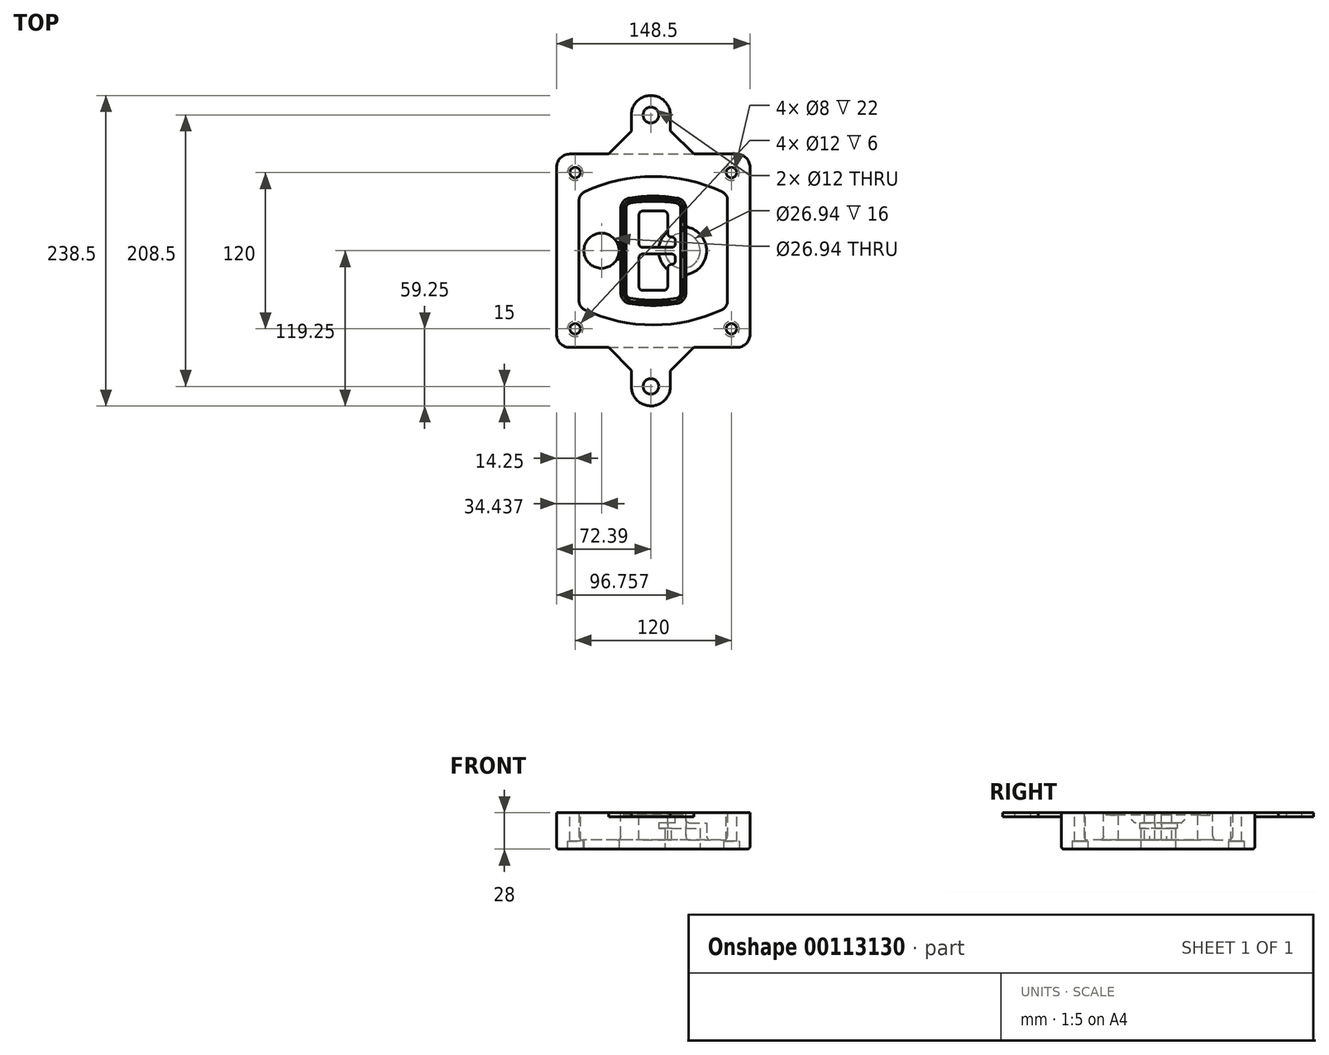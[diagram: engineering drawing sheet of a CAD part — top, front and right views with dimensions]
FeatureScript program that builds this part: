
annotation { "Feature Type Name" : "Feature", "Feature Type Description" : "" }
export const myFeature = defineFeature(function(context is Context, id is Id, definition is map)
    precondition{}
    {
        {
            var Q0;
            Q0=qCreatedBy(makeId("Top.planeOp"),FACE);
            var sketch = newSketch(context, id + "F0", { "sketchPlane" : qUnion([Q0])});
            skPoint(sketch, "E0.rect.middle", {"position": v(0, 0) * mm});
            skLineSegment(sketch, "E1.bottom", {"start": v(-64.25, -74.25) * mm, "end": v(64.25, -74.25) * mm});
            skLineSegment(sketch, "E1.top", {"start": v(-64.25, 74.25) * mm, "end": v(64.25, 74.25) * mm});
            skLineSegment(sketch, "E1.left", {"start": v(-74.25, -64.25) * mm, "end": v(-74.25, 64.25) * mm});
            skLineSegment(sketch, "E1.right", {"start": v(74.25, -64.25) * mm, "end": v(74.25, 64.25) * mm});
            skLineSegment(sketch, "E2", {"start": v(-74.25, 74.25) * mm, "end": v(74.25, -74.25) * mm, "construction": true});
            skLineSegment(sketch, "E3", {"start": v(74.25, 74.25) * mm, "end": v(-74.25, -74.25) * mm, "construction": true});
            skCircle(sketch, "E4", {"center": v(-60, 60) * mm, "radius": 4 * mm});
            skCircle(sketch, "E5", {"center": v(60, 60) * mm, "radius": 4 * mm});
            skCircle(sketch, "E6", {"center": v(60, -60) * mm, "radius": 4 * mm});
            skCircle(sketch, "E7", {"center": v(-60, -60) * mm, "radius": 4 * mm});
            skLineSegment(sketch, "E8", {"start": v(-60, 60) * mm, "end": v(60, 60) * mm, "construction": true});
            skLineSegment(sketch, "E9", {"start": v(60, 60) * mm, "end": v(60, -60) * mm, "construction": true});
            skLineSegment(sketch, "E10", {"start": v(60, -60) * mm, "end": v(-60, -60) * mm, "construction": true});
            skLineSegment(sketch, "E11", {"start": v(-60, -60) * mm, "end": v(-60, 60) * mm, "construction": true});
            skLineSegment(sketch, "E12", {"start": v(-60, 38.83) * mm, "end": v(-60, -38.83) * mm});
            skLineSegment(sketch, "E13", {"start": v(60, 38.83) * mm, "end": v(60, -38.83) * mm});
            skArc(sketch, "E14", {"start": v(54.26, 47.88) * mm, "mid": v(0, 60) * mm, "end": v(-54.26, 47.88) * mm});
            skArc(sketch, "E15", {"start": v(-54.26, -47.88) * mm, "mid": v(0, -60) * mm, "end": v(54.26, -47.88) * mm});
            skLineSegment(sketch, "E16", {"start": v(-60, 0) * mm, "end": v(60, 0) * mm, "construction": true});
            skPoint(sketch, "E17.visualSharp", {"position": v(-60, -45) * mm});
            skArc(sketch, "E17.filletArc", {"start": v(-60, -38.83) * mm, "mid": v(-58.44, -44.2) * mm, "end": v(-54.26, -47.88) * mm});
            skPoint(sketch, "E18.visualSharp", {"position": v(-60, 45) * mm});
            skArc(sketch, "E18.filletArc", {"start": v(-54.26, 47.88) * mm, "mid": v(-58.44, 44.2) * mm, "end": v(-60, 38.83) * mm});
            skPoint(sketch, "E19.visualSharp", {"position": v(60, 45) * mm});
            skArc(sketch, "E19.filletArc", {"start": v(60, 38.83) * mm, "mid": v(58.44, 44.2) * mm, "end": v(54.26, 47.88) * mm});
            skPoint(sketch, "E20.visualSharp", {"position": v(60, -45) * mm});
            skArc(sketch, "E20.filletArc", {"start": v(54.26, -47.88) * mm, "mid": v(58.44, -44.2) * mm, "end": v(60, -38.83) * mm});
            skPoint(sketch, "E21.visualSharp", {"position": v(-74.25, 74.25) * mm});
            skArc(sketch, "E21.filletArc", {"start": v(-64.25, 74.25) * mm, "mid": v(-71.32, 71.32) * mm, "end": v(-74.25, 64.25) * mm});
            skPoint(sketch, "E22.visualSharp", {"position": v(74.25, 74.25) * mm});
            skArc(sketch, "E22.filletArc", {"start": v(74.25, 64.25) * mm, "mid": v(71.32, 71.32) * mm, "end": v(64.25, 74.25) * mm});
            skPoint(sketch, "E23.visualSharp", {"position": v(74.25, -74.25) * mm});
            skArc(sketch, "E23.filletArc", {"start": v(64.25, -74.25) * mm, "mid": v(71.32, -71.32) * mm, "end": v(74.25, -64.25) * mm});
            skPoint(sketch, "E24.visualSharp", {"position": v(-74.25, -74.25) * mm});
            skArc(sketch, "E24.filletArc", {"start": v(-74.25, -64.25) * mm, "mid": v(-71.32, -71.32) * mm, "end": v(-64.25, -74.25) * mm});
            skArc(sketch, "E25.0", {"start": v(57, 38.83) * mm, "mid": v(55.9, 42.58) * mm, "end": v(52.98, 45.17) * mm});
            skLineSegment(sketch, "E25.1", {"start": v(57, 38.83) * mm, "end": v(57, -38.83) * mm});
            skArc(sketch, "E25.2", {"start": v(52.98, -45.17) * mm, "mid": v(55.9, -42.58) * mm, "end": v(57, -38.83) * mm});
            skArc(sketch, "E25.3", {"start": v(-52.98, -45.17) * mm, "mid": v(0, -57) * mm, "end": v(52.98, -45.17) * mm});
            skArc(sketch, "E25.4", {"start": v(-57, -38.83) * mm, "mid": v(-55.9, -42.58) * mm, "end": v(-52.98, -45.17) * mm});
            skArc(sketch, "E25.5", {"start": v(52.98, 45.17) * mm, "mid": v(0, 57) * mm, "end": v(-52.98, 45.17) * mm});
            skLineSegment(sketch, "E25.6", {"start": v(-57, 38.83) * mm, "end": v(-57, -38.83) * mm});
            skArc(sketch, "E25.7", {"start": v(-52.98, 45.17) * mm, "mid": v(-55.9, 42.58) * mm, "end": v(-57, 38.83) * mm});
            skArc(sketch, "E26.0", {"start": v(-55.96, 51.5) * mm, "mid": v(-61.82, 46.33) * mm, "end": v(-64, 38.83) * mm});
            skArc(sketch, "E26.1", {"start": v(55.96, 51.5) * mm, "mid": v(0, 64) * mm, "end": v(-55.96, 51.5) * mm});
            skArc(sketch, "E26.2", {"start": v(64, 38.83) * mm, "mid": v(61.82, 46.33) * mm, "end": v(55.96, 51.5) * mm});
            skLineSegment(sketch, "E26.3", {"start": v(64, 38.83) * mm, "end": v(64, -38.83) * mm});
            skArc(sketch, "E26.4", {"start": v(55.96, -51.5) * mm, "mid": v(61.82, -46.33) * mm, "end": v(64, -38.83) * mm});
            skLineSegment(sketch, "E26.5", {"start": v(-64, 38.83) * mm, "end": v(-64, -38.83) * mm});
            skArc(sketch, "E26.6", {"start": v(-55.96, -51.5) * mm, "mid": v(0, -64) * mm, "end": v(55.96, -51.5) * mm});
            skArc(sketch, "E26.7", {"start": v(-64, -38.83) * mm, "mid": v(-61.82, -46.33) * mm, "end": v(-55.96, -51.5) * mm});
            skSolve(sketch);
        }
        {
            var Q0;
            Q0=makeQuery(id+"F0.imprint","IMPRINT",FACE,{"disambiguationData":[TD([[makeQuery(id+"F0.imprint","IMPRINT",EDGE,{"derivedFrom":sQuery(id+"F0.wireOp",EDGE,"E1.bottom")}),1.0]])]});
            var Q1;
            Q1=makeQuery(id+"F0.imprint","IMPRINT",FACE,{"disambiguationData":[TD([[makeQuery(id+"F0.imprint","IMPRINT",EDGE,{"derivedFrom":sQuery(id+"F0.wireOp",EDGE,"E12")}),1.0]])]});
            var Q2;
            Q2=makeQuery(id+"F0.imprint","IMPRINT",FACE,{"disambiguationData":[TD([[makeQuery(id+"F0.imprint","IMPRINT",EDGE,{"derivedFrom":sQuery(id+"F0.wireOp",EDGE,"E25.0")}),1.0]])]});
            var Q3;
            Q3=makeQuery(id+"F0.imprint","IMPRINT",FACE,{"disambiguationData":[TD([[makeQuery(id+"F0.imprint","IMPRINT",EDGE,{"derivedFrom":sQuery(id+"F0.wireOp",EDGE,"E12")}),-1.0]])]});
            extrude(context, id + "F1", {"entities" : qUnion([Q0, Q1, Q2, Q3]), "oppositeDirection" : true, "depth" : 25 * mm});
        }
        {
            var Q0;
            Q0=makeQuery(id+"F0.imprint","IMPRINT",FACE,{"disambiguationData":[TD([[makeQuery(id+"F0.imprint","IMPRINT",EDGE,{"derivedFrom":sQuery(id+"F0.wireOp",EDGE,"E12")}),1.0]])]});
            extrude(context, id + "F2", {"entities" : qUnion([Q0]), "operationType" : NewBodyOperationType.ADD, "depth" : 3 * mm});
        }
        {
            var Q0;
            Q0=makeQuery(id+"F0.imprint","IMPRINT",FACE,{"disambiguationData":[TD([[makeQuery(id+"F0.imprint","IMPRINT",EDGE,{"derivedFrom":sQuery(id+"F0.wireOp",EDGE,"E25.0")}),1.0]])]});
            extrude(context, id + "F3", {"entities" : qUnion([Q0]), "operationType" : NewBodyOperationType.REMOVE, "oppositeDirection" : true, "depth" : 18 * mm});
        }
        {
            var Q0;
            Q0=makeQuery(id+"F2.opExtrude","CAP_FACE",FACE,{"disambiguationData":[OSD([sQuery(id+"F0.wireOp",EDGE,"E12"),sQuery(id+"F0.wireOp",EDGE,"E13"),sQuery(id+"F0.wireOp",EDGE,"E14"),sQuery(id+"F0.wireOp",EDGE,"E15"),sQuery(id+"F0.wireOp",EDGE,"E17.filletArc"),sQuery(id+"F0.wireOp",EDGE,"E18.filletArc"),sQuery(id+"F0.wireOp",EDGE,"E19.filletArc"),sQuery(id+"F0.wireOp",EDGE,"E20.filletArc"),sQuery(id+"F0.wireOp",EDGE,"E25.0"),sQuery(id+"F0.wireOp",EDGE,"E25.1"),sQuery(id+"F0.wireOp",EDGE,"E25.2"),sQuery(id+"F0.wireOp",EDGE,"E25.3"),sQuery(id+"F0.wireOp",EDGE,"E25.4"),sQuery(id+"F0.wireOp",EDGE,"E25.5"),sQuery(id+"F0.wireOp",EDGE,"E25.6"),sQuery(id+"F0.wireOp",EDGE,"E25.7")])],"isStart":false});
            var sketch = newSketch(context, id + "F4", { "sketchPlane" : qUnion([Q0])});
            skArc(sketch, "E27.0", {"start": v(-18.34, -40.45) * mm, "mid": v(0, -42) * mm, "end": v(18.34, -40.45) * mm});
            skArc(sketch, "E28.0", {"start": v(18.34, 40.45) * mm, "mid": v(0, 42) * mm, "end": v(-18.34, 40.45) * mm});
            skLineSegment(sketch, "E29", {"start": v(-25, 32.57) * mm, "end": v(-25, -32.57) * mm});
            skLineSegment(sketch, "E30", {"start": v(25, 32.57) * mm, "end": v(25, -32.57) * mm});
            skLineSegment(sketch, "E31", {"start": v(-25, 39.1) * mm, "end": v(25, 39.1) * mm, "construction": true});
            skLineSegment(sketch, "E32", {"start": v(-25, -39.1) * mm, "end": v(25, -39.1) * mm, "construction": true});
            skPoint(sketch, "E33.visualSharp", {"position": v(-25, 39.1) * mm});
            skArc(sketch, "E33.filletArc", {"start": v(-18.34, 40.45) * mm, "mid": v(-23.11, 37.73) * mm, "end": v(-25, 32.57) * mm});
            skPoint(sketch, "E34.visualSharp", {"position": v(25, 39.1) * mm});
            skArc(sketch, "E34.filletArc", {"start": v(25, 32.57) * mm, "mid": v(23.11, 37.73) * mm, "end": v(18.34, 40.45) * mm});
            skPoint(sketch, "E35.visualSharp", {"position": v(25, -39.1) * mm});
            skArc(sketch, "E35.filletArc", {"start": v(18.34, -40.45) * mm, "mid": v(23.11, -37.73) * mm, "end": v(25, -32.57) * mm});
            skPoint(sketch, "E36.visualSharp", {"position": v(-25, -39.1) * mm});
            skArc(sketch, "E36.filletArc", {"start": v(-25, -32.57) * mm, "mid": v(-23.11, -37.73) * mm, "end": v(-18.34, -40.45) * mm});
            skArc(sketch, "E37.0", {"start": v(52.98, 45.17) * mm, "mid": v(0, 57) * mm, "end": v(-52.98, 45.17) * mm});
            skArc(sketch, "E37.1", {"start": v(-52.98, 45.17) * mm, "mid": v(-55.9, 42.58) * mm, "end": v(-57, 38.83) * mm});
            skLineSegment(sketch, "E37.2", {"start": v(-57, 38.83) * mm, "end": v(-57, -38.83) * mm});
            skArc(sketch, "E37.3", {"start": v(-57, -38.83) * mm, "mid": v(-55.9, -42.58) * mm, "end": v(-52.98, -45.17) * mm});
            skArc(sketch, "E37.4", {"start": v(-52.98, -45.17) * mm, "mid": v(0, -57) * mm, "end": v(52.98, -45.17) * mm});
            skArc(sketch, "E37.5", {"start": v(52.98, -45.17) * mm, "mid": v(55.9, -42.58) * mm, "end": v(57, -38.83) * mm});
            skLineSegment(sketch, "E37.6", {"start": v(57, 38.83) * mm, "end": v(57, -38.83) * mm});
            skArc(sketch, "E37.7", {"start": v(57, 38.83) * mm, "mid": v(55.9, 42.58) * mm, "end": v(52.98, 45.17) * mm});
            skLineSegment(sketch, "E38.0", {"start": v(23, 32.57) * mm, "end": v(23, -32.57) * mm});
            skArc(sketch, "E38.1", {"start": v(18, -38.48) * mm, "mid": v(21.58, -36.44) * mm, "end": v(23, -32.57) * mm});
            skArc(sketch, "E38.2", {"start": v(-18, -38.48) * mm, "mid": v(0, -40) * mm, "end": v(18, -38.48) * mm});
            skArc(sketch, "E38.3", {"start": v(-23, -32.57) * mm, "mid": v(-21.58, -36.44) * mm, "end": v(-18, -38.48) * mm});
            skLineSegment(sketch, "E38.4", {"start": v(-23, 32.57) * mm, "end": v(-23, -32.57) * mm});
            skArc(sketch, "E38.5", {"start": v(23, 32.57) * mm, "mid": v(21.58, 36.44) * mm, "end": v(18, 38.48) * mm});
            skArc(sketch, "E38.6", {"start": v(-18, 38.48) * mm, "mid": v(-21.58, 36.44) * mm, "end": v(-23, 32.57) * mm});
            skArc(sketch, "E38.7", {"start": v(18, 38.48) * mm, "mid": v(0, 40) * mm, "end": v(-18, 38.48) * mm});
            skArc(sketch, "E39.0", {"start": v(21, 32.57) * mm, "mid": v(20.06, 35.15) * mm, "end": v(17.67, 36.5) * mm});
            skLineSegment(sketch, "E39.1", {"start": v(21, 32.57) * mm, "end": v(21, -32.57) * mm});
            skArc(sketch, "E39.2", {"start": v(17.67, -36.5) * mm, "mid": v(20.06, -35.15) * mm, "end": v(21, -32.57) * mm});
            skArc(sketch, "E39.3", {"start": v(-17.67, -36.5) * mm, "mid": v(0, -38) * mm, "end": v(17.67, -36.5) * mm});
            skArc(sketch, "E39.4", {"start": v(-21, -32.57) * mm, "mid": v(-20.06, -35.15) * mm, "end": v(-17.67, -36.5) * mm});
            skArc(sketch, "E39.5", {"start": v(17.67, 36.5) * mm, "mid": v(0, 38) * mm, "end": v(-17.67, 36.5) * mm});
            skLineSegment(sketch, "E39.6", {"start": v(-21, 32.57) * mm, "end": v(-21, -32.57) * mm});
            skArc(sketch, "E39.7", {"start": v(-17.67, 36.5) * mm, "mid": v(-20.06, 35.15) * mm, "end": v(-21, 32.57) * mm});
            skLineSegment(sketch, "E40", {"start": v(-25, 0) * mm, "end": v(25, 0) * mm, "construction": true});
            skLineSegment(sketch, "E41", {"start": v(-11, 5.5) * mm, "end": v(-11, 27.5) * mm});
            skLineSegment(sketch, "E42", {"start": v(-8, 30.5) * mm, "end": v(8, 30.5) * mm});
            skLineSegment(sketch, "E43", {"start": v(11, 27.5) * mm, "end": v(11, 13.5) * mm});
            skLineSegment(sketch, "E44", {"start": v(14, 10.5) * mm, "end": v(14, 10.5) * mm});
            skLineSegment(sketch, "E45", {"start": v(17, 7.5) * mm, "end": v(17, 5.5) * mm});
            skLineSegment(sketch, "E46", {"start": v(14, 2.5) * mm, "end": v(-8, 2.5) * mm});
            skPoint(sketch, "E47.visualSharp", {"position": v(-11, 30.5) * mm});
            skArc(sketch, "E47.filletArc", {"start": v(-8, 30.5) * mm, "mid": v(-10.12, 29.62) * mm, "end": v(-11, 27.5) * mm});
            skPoint(sketch, "E48.visualSharp", {"position": v(11, 30.5) * mm});
            skArc(sketch, "E48.filletArc", {"start": v(11, 27.5) * mm, "mid": v(10.12, 29.62) * mm, "end": v(8, 30.5) * mm});
            skPoint(sketch, "E49.visualSharp", {"position": v(11, 10.5) * mm});
            skArc(sketch, "E49.filletArc", {"start": v(11, 13.5) * mm, "mid": v(11.88, 11.38) * mm, "end": v(14, 10.5) * mm});
            skPoint(sketch, "E50.visualSharp", {"position": v(17, 10.5) * mm});
            skArc(sketch, "E50.filletArc", {"start": v(17, 7.5) * mm, "mid": v(16.12, 9.62) * mm, "end": v(14, 10.5) * mm});
            skPoint(sketch, "E51.visualSharp", {"position": v(17, 2.5) * mm});
            skArc(sketch, "E51.filletArc", {"start": v(14, 2.5) * mm, "mid": v(16.12, 3.38) * mm, "end": v(17, 5.5) * mm});
            skPoint(sketch, "E52.visualSharp", {"position": v(-11, 2.5) * mm});
            skArc(sketch, "E52.filletArc", {"start": v(-11, 5.5) * mm, "mid": v(-10.12, 3.38) * mm, "end": v(-8, 2.5) * mm});
            skLineSegment(sketch, "E53.0.MirrorCS", {"start": v(14, -2.5) * mm, "end": v(-8, -2.5) * mm});
            skArc(sketch, "E54.0.MirrorCS", {"start": v(-11, -5.5) * mm, "mid": v(-10.12, -3.38) * mm, "end": v(-8, -2.5) * mm});
            skLineSegment(sketch, "E55.0.MirrorCS", {"start": v(-11, -5.5) * mm, "end": v(-11, -27.5) * mm});
            skArc(sketch, "E56.0.MirrorCS", {"start": v(-8, -30.5) * mm, "mid": v(-10.12, -29.62) * mm, "end": v(-11, -27.5) * mm});
            skLineSegment(sketch, "E57.0.MirrorCS", {"start": v(-8, -30.5) * mm, "end": v(8, -30.5) * mm});
            skArc(sketch, "E58.0.MirrorCS", {"start": v(11, -27.5) * mm, "mid": v(10.12, -29.62) * mm, "end": v(8, -30.5) * mm});
            skLineSegment(sketch, "E59.0.MirrorCS", {"start": v(11, -27.5) * mm, "end": v(11, -13.5) * mm});
            skArc(sketch, "E60.0.MirrorCS", {"start": v(11, -13.5) * mm, "mid": v(11.88, -11.38) * mm, "end": v(14, -10.5) * mm});
            skArc(sketch, "E61.0.MirrorCS", {"start": v(17, -7.5) * mm, "mid": v(16.12, -9.62) * mm, "end": v(14, -10.5) * mm});
            skLineSegment(sketch, "E62.0.MirrorCS", {"start": v(17, -7.5) * mm, "end": v(17, -5.5) * mm});
            skArc(sketch, "E63.0.MirrorCS", {"start": v(14, -2.5) * mm, "mid": v(16.12, -3.38) * mm, "end": v(17, -5.5) * mm});
            skSolve(sketch);
        }
        {
            var Q0;
            Q0=makeQuery(id+"F4.imprint","IMPRINT",FACE,{"disambiguationData":[TD([[makeQuery(id+"F4.imprint","IMPRINT",EDGE,{"derivedFrom":sQuery(id+"F4.wireOp",EDGE,"E27.0")}),1.0]])]});
            var Q1;
            Q1=makeQuery(id+"F4.imprint","IMPRINT",FACE,{"disambiguationData":[TD([[makeQuery(id+"F4.imprint","IMPRINT",EDGE,{"derivedFrom":sQuery(id+"F4.wireOp",EDGE,"E38.0")}),-1.0]])]});
            var Q2;
            Q2=makeQuery(id+"F4.imprint","IMPRINT",FACE,{"disambiguationData":[TD([[makeQuery(id+"F4.imprint","IMPRINT",EDGE,{"derivedFrom":sQuery(id+"F4.wireOp",EDGE,"E39.0")}),1.0]])]});
            extrude(context, id + "F5", {"entities" : qUnion([Q0, Q1, Q2]), "operationType" : NewBodyOperationType.ADD, "endBound" : BoundingType.UP_TO_NEXT, "oppositeDirection" : true, "depth" : 25 * mm});
        }
        {
            var Q0;
            Q0=makeQuery(id+"F4.imprint","IMPRINT",FACE,{"disambiguationData":[TD([[makeQuery(id+"F4.imprint","IMPRINT",EDGE,{"derivedFrom":sQuery(id+"F4.wireOp",EDGE,"E38.0")}),-1.0]])]});
            extrude(context, id + "F6", {"entities" : qUnion([Q0]), "operationType" : NewBodyOperationType.REMOVE, "oppositeDirection" : true, "depth" : 2 * mm});
        }
        {
            var Q0;
            Q0=makeQuery(id+"F1.opExtrude","CAP_FACE",FACE,{"disambiguationData":[OSD([sQuery(id+"F0.wireOp",EDGE,"E1.bottom"),sQuery(id+"F0.wireOp",EDGE,"E1.top"),sQuery(id+"F0.wireOp",EDGE,"E1.left"),sQuery(id+"F0.wireOp",EDGE,"E1.right"),sQuery(id+"F0.wireOp",EDGE,"E4"),sQuery(id+"F0.wireOp",EDGE,"E5"),sQuery(id+"F0.wireOp",EDGE,"E6"),sQuery(id+"F0.wireOp",EDGE,"E7"),sQuery(id+"F0.wireOp",EDGE,"E21.filletArc"),sQuery(id+"F0.wireOp",EDGE,"E22.filletArc"),sQuery(id+"F0.wireOp",EDGE,"E23.filletArc"),sQuery(id+"F0.wireOp",EDGE,"E24.filletArc")])],"isStart":false});
            var sketch = newSketch(context, id + "F7", { "sketchPlane" : qUnion([Q0])});
            skCircle(sketch, "E64", {"center": v(22.5, 0) * mm, "radius": 13.47 * mm});
            skCircle(sketch, "E65", {"center": v(-39.81, 0) * mm, "radius": 13.47 * mm});
            skLineSegment(sketch, "E66", {"start": v(74.25, 0) * mm, "end": v(-74.25, 0) * mm});
            skCircle(sketch, "E67", {"center": v(22.5, 0) * mm, "radius": 18.47 * mm});
            skCircle(sketch, "E68", {"center": v(60, -60) * mm, "radius": 6 * mm});
            skCircle(sketch, "E69", {"center": v(-60, -60) * mm, "radius": 6 * mm});
            skCircle(sketch, "E70", {"center": v(-60, 60) * mm, "radius": 6 * mm});
            skCircle(sketch, "E71", {"center": v(60, 60) * mm, "radius": 6 * mm});
            skSolve(sketch);
        }
        {
            var Q0;
            {var subQ1=sQuery(id+"F7.wireOp",EDGE,"E66");var subQ4=sQuery(id+"F7.wireOp",EDGE,"E64");var subQ6=makeQuery(id+"F7.imprint","INTERSECT",VERTEX,{"disambiguationData":[OD(0.0)],"derivedFrom":[subQ4,subQ1]});Q0=makeQuery(id+"F7.imprint","IMPRINT",FACE,{"disambiguationData":[TD([[makeQuery(id+"F7.imprint","IMPRINT",EDGE,{"disambiguationData":[TD([[subQ6,-1.0]])],"derivedFrom":subQ4}),-1.0]])]});}
            var Q1;
            {var subQ0=sQuery(id+"F7.wireOp",EDGE,"E66");var subQ1=sQuery(id+"F7.wireOp",EDGE,"E64");var subQ3=makeQuery(id+"F7.imprint","INTERSECT",VERTEX,{"disambiguationData":[OD(0.0)],"derivedFrom":[subQ1,subQ0]});Q1=makeQuery(id+"F7.imprint","IMPRINT",FACE,{"disambiguationData":[TD([[makeQuery(id+"F7.imprint","IMPRINT",EDGE,{"disambiguationData":[TD([[subQ3,-1.0]])],"derivedFrom":subQ1}),1.0]])]});}
            var Q2;
            {var subQ0=sQuery(id+"F7.wireOp",EDGE,"E66");var subQ1=sQuery(id+"F7.wireOp",EDGE,"E64");var subQ3=makeQuery(id+"F7.imprint","INTERSECT",VERTEX,{"disambiguationData":[OD(0.0)],"derivedFrom":[subQ1,subQ0]});Q2=makeQuery(id+"F7.imprint","IMPRINT",FACE,{"disambiguationData":[TD([[makeQuery(id+"F7.imprint","IMPRINT",EDGE,{"disambiguationData":[TD([[subQ3,1.0]])],"derivedFrom":subQ1}),1.0]])]});}
            var Q3;
            {var subQ1=sQuery(id+"F7.wireOp",EDGE,"E66");var subQ4=sQuery(id+"F7.wireOp",EDGE,"E64");var subQ6=makeQuery(id+"F7.imprint","INTERSECT",VERTEX,{"disambiguationData":[OD(0.0)],"derivedFrom":[subQ4,subQ1]});Q3=makeQuery(id+"F7.imprint","IMPRINT",FACE,{"disambiguationData":[TD([[makeQuery(id+"F7.imprint","IMPRINT",EDGE,{"disambiguationData":[TD([[subQ6,1.0]])],"derivedFrom":subQ4}),-1.0]])]});}
            extrude(context, id + "F8", {"entities" : qUnion([Q0, Q1, Q2, Q3]), "operationType" : NewBodyOperationType.ADD, "oppositeDirection" : true, "depth" : 20 * mm});
        }
        {
            var Q0;
            {var subQ0=sQuery(id+"F7.wireOp",EDGE,"E66");var subQ1=sQuery(id+"F7.wireOp",EDGE,"E64");var subQ3=makeQuery(id+"F7.imprint","INTERSECT",VERTEX,{"disambiguationData":[OD(0.0)],"derivedFrom":[subQ1,subQ0]});Q0=makeQuery(id+"F7.imprint","IMPRINT",FACE,{"disambiguationData":[TD([[makeQuery(id+"F7.imprint","IMPRINT",EDGE,{"disambiguationData":[TD([[subQ3,-1.0]])],"derivedFrom":subQ1}),1.0]])]});}
            var Q1;
            {var subQ0=sQuery(id+"F7.wireOp",EDGE,"E66");var subQ1=sQuery(id+"F7.wireOp",EDGE,"E64");var subQ3=makeQuery(id+"F7.imprint","INTERSECT",VERTEX,{"disambiguationData":[OD(0.0)],"derivedFrom":[subQ1,subQ0]});Q1=makeQuery(id+"F7.imprint","IMPRINT",FACE,{"disambiguationData":[TD([[makeQuery(id+"F7.imprint","IMPRINT",EDGE,{"disambiguationData":[TD([[subQ3,1.0]])],"derivedFrom":subQ1}),1.0]])]});}
            extrude(context, id + "F9", {"entities" : qUnion([Q0, Q1]), "operationType" : NewBodyOperationType.REMOVE, "oppositeDirection" : true, "depth" : 16 * mm});
        }
        {
            var Q0;
            {var subQ0=sQuery(id+"F7.wireOp",EDGE,"E66");var subQ1=sQuery(id+"F7.wireOp",EDGE,"E65");var subQ3=makeQuery(id+"F7.imprint","INTERSECT",VERTEX,{"disambiguationData":[OD(0.0)],"derivedFrom":[subQ1,subQ0]});Q0=makeQuery(id+"F7.imprint","IMPRINT",FACE,{"disambiguationData":[TD([[makeQuery(id+"F7.imprint","IMPRINT",EDGE,{"disambiguationData":[TD([[subQ3,-1.0]])],"derivedFrom":subQ1}),1.0]])]});}
            var Q1;
            {var subQ0=sQuery(id+"F7.wireOp",EDGE,"E66");var subQ1=sQuery(id+"F7.wireOp",EDGE,"E65");var subQ3=makeQuery(id+"F7.imprint","INTERSECT",VERTEX,{"disambiguationData":[OD(0.0)],"derivedFrom":[subQ1,subQ0]});Q1=makeQuery(id+"F7.imprint","IMPRINT",FACE,{"disambiguationData":[TD([[makeQuery(id+"F7.imprint","IMPRINT",EDGE,{"disambiguationData":[TD([[subQ3,1.0]])],"derivedFrom":subQ1}),1.0]])]});}
            extrude(context, id + "F10", {"entities" : qUnion([Q0, Q1]), "operationType" : NewBodyOperationType.REMOVE, "oppositeDirection" : true, "depth" : 25 * mm});
        }
        {
            var Q0;
            Q0=makeQuery(id+"F7.imprint","IMPRINT",FACE,{"disambiguationData":[TD([[makeQuery(id+"F7.imprint","IMPRINT",EDGE,{"derivedFrom":sQuery(id+"F7.wireOp",EDGE,"E68")}),1.0]])]});
            var Q1;
            Q1=makeQuery(id+"F7.imprint","IMPRINT",FACE,{"disambiguationData":[TD([[makeQuery(id+"F7.imprint","IMPRINT",EDGE,{"derivedFrom":makeQuery(id+"F1.opExtrude","CAP_EDGE",EDGE,{"disambiguationData":[OSD([sQuery(id+"F0.wireOp",EDGE,"E5")])],"isStart":false})}),-1.0]])]});
            var Q2;
            Q2=makeQuery(id+"F7.imprint","IMPRINT",FACE,{"disambiguationData":[TD([[makeQuery(id+"F7.imprint","IMPRINT",EDGE,{"derivedFrom":sQuery(id+"F7.wireOp",EDGE,"E69")}),1.0]])]});
            var Q3;
            Q3=makeQuery(id+"F7.imprint","IMPRINT",FACE,{"disambiguationData":[TD([[makeQuery(id+"F7.imprint","IMPRINT",EDGE,{"derivedFrom":makeQuery(id+"F1.opExtrude","CAP_EDGE",EDGE,{"disambiguationData":[OSD([sQuery(id+"F0.wireOp",EDGE,"E4")])],"isStart":false})}),-1.0]])]});
            var Q4;
            Q4=makeQuery(id+"F7.imprint","IMPRINT",FACE,{"disambiguationData":[TD([[makeQuery(id+"F7.imprint","IMPRINT",EDGE,{"derivedFrom":sQuery(id+"F7.wireOp",EDGE,"E70")}),1.0]])]});
            var Q5;
            Q5=makeQuery(id+"F7.imprint","IMPRINT",FACE,{"disambiguationData":[TD([[makeQuery(id+"F7.imprint","IMPRINT",EDGE,{"derivedFrom":makeQuery(id+"F1.opExtrude","CAP_EDGE",EDGE,{"disambiguationData":[OSD([sQuery(id+"F0.wireOp",EDGE,"E7")])],"isStart":false})}),-1.0]])]});
            var Q6;
            Q6=makeQuery(id+"F7.imprint","IMPRINT",FACE,{"disambiguationData":[TD([[makeQuery(id+"F7.imprint","IMPRINT",EDGE,{"derivedFrom":sQuery(id+"F7.wireOp",EDGE,"E71")}),1.0]])]});
            var Q7;
            Q7=makeQuery(id+"F7.imprint","IMPRINT",FACE,{"disambiguationData":[TD([[makeQuery(id+"F7.imprint","IMPRINT",EDGE,{"derivedFrom":makeQuery(id+"F1.opExtrude","CAP_EDGE",EDGE,{"disambiguationData":[OSD([sQuery(id+"F0.wireOp",EDGE,"E6")])],"isStart":false})}),-1.0]])]});
            extrude(context, id + "F11", {"entities" : qUnion([Q0, Q1, Q2, Q3, Q4, Q5, Q6, Q7]), "operationType" : NewBodyOperationType.REMOVE, "oppositeDirection" : true, "depth" : 6 * mm});
        }
        {
            var Q0;
            Q0=makeQuery(id+"F9.boolean.opBoolean","COPY",FACE,{"derivedFrom":makeQuery(id+"F9.opExtrude","CAP_FACE",FACE,{"disambiguationData":[OSD([sQuery(id+"F7.wireOp",EDGE,"E64")])],"isStart":false})});
            var sketch = newSketch(context, id + "F12", { "sketchPlane" : qUnion([Q0])});
            skArc(sketch, "E72.0", {"start": v(11, 14.45) * mm, "mid": v(6.45, 9.13) * mm, "end": v(4.2, 2.5) * mm});
            skArc(sketch, "E72.1", {"start": v(4.2, -2.5) * mm, "mid": v(6.45, -9.13) * mm, "end": v(11, -14.45) * mm});
            skLineSegment(sketch, "E73", {"start": v(4.2, -2.5) * mm, "end": v(14, -2.5) * mm});
            skLineSegment(sketch, "E74.0", {"start": v(14, 2.5) * mm, "end": v(4.2, 2.5) * mm});
            skArc(sketch, "E74.1", {"start": v(14, 2.5) * mm, "mid": v(16.12, 3.38) * mm, "end": v(17, 5.5) * mm});
            skLineSegment(sketch, "E74.2", {"start": v(17, 7.5) * mm, "end": v(17, 5.5) * mm});
            skArc(sketch, "E74.3", {"start": v(17, 7.5) * mm, "mid": v(16.12, 9.62) * mm, "end": v(14, 10.5) * mm});
            skArc(sketch, "E74.4", {"start": v(11, 13.5) * mm, "mid": v(11.88, 11.38) * mm, "end": v(14, 10.5) * mm});
            skLineSegment(sketch, "E74.5", {"start": v(11, 14.45) * mm, "end": v(11, 13.5) * mm});
            skLineSegment(sketch, "E74.7", {"start": v(14, -2.5) * mm, "end": v(4.2, -2.5) * mm});
            skArc(sketch, "E74.8", {"start": v(14, -2.5) * mm, "mid": v(16.12, -3.38) * mm, "end": v(17, -5.5) * mm});
            skLineSegment(sketch, "E74.9", {"start": v(17, -7.5) * mm, "end": v(17, -5.5) * mm});
            skArc(sketch, "E74.10", {"start": v(17, -7.5) * mm, "mid": v(16.12, -9.62) * mm, "end": v(14, -10.5) * mm});
            skArc(sketch, "E74.11", {"start": v(11, -13.5) * mm, "mid": v(11.88, -11.38) * mm, "end": v(14, -10.5) * mm});
            skLineSegment(sketch, "E74.12", {"start": v(11, -14.45) * mm, "end": v(11, -13.5) * mm});
            skPoint(sketch, "E75.orphan", {"position": v(11, -27.5) * mm});
            skPoint(sketch, "E76.orphan", {"position": v(-8, -2.5) * mm});
            skPoint(sketch, "E77.orphan", {"position": v(-8, 2.5) * mm});
            skPoint(sketch, "E78.orphan", {"position": v(11, 27.5) * mm});
            skSolve(sketch);
        }
        {
            var Q0;
            {var subQ7=sQuery(id+"F12.wireOp",EDGE,"E72.0");var subQ14=sQuery(id+"F12.wireOp",EDGE,"E72.1");var subQ16=sQuery(id+"F12.wireOp",EDGE,"E74.1");var subQ18=sQuery(id+"F12.wireOp",EDGE,"E74.8");Q0=qUnion([makeQuery(id+"F12.imprint","IMPRINT",FACE,{"disambiguationData":[TD([[makeQuery(id+"F12.imprint","IMPRINT",EDGE,{"derivedFrom":subQ7}),1.0]])]}),makeQuery(id+"F12.imprint","IMPRINT",FACE,{"disambiguationData":[TD([[makeQuery(id+"F12.imprint","IMPRINT",EDGE,{"derivedFrom":subQ14}),1.0]])]}),makeQuery(id+"F12.imprint","IMPRINT",FACE,{"disambiguationData":[TD([[makeQuery(id+"F12.imprint","IMPRINT",EDGE,{"derivedFrom":subQ16}),1.0]])]}),makeQuery(id+"F12.imprint","IMPRINT",FACE,{"disambiguationData":[TD([[makeQuery(id+"F12.imprint","IMPRINT",EDGE,{"derivedFrom":subQ18}),-1.0]])]})]);}
            var Q1;
            Q1=makeQuery(id+"F5.boolean.opBoolean","SPLIT",FACE,{"disambiguationData":[TD([makeQuery(id+"F5.opExtrude","SWEPT_FACE",FACE,{"disambiguationData":[OSD([sQuery(id+"F4.wireOp",EDGE,"E41")])]})])],"derivedFrom":makeQuery(id+"F3.boolean.opBoolean","COPY",FACE,{"derivedFrom":makeQuery(id+"F3.opExtrude","CAP_FACE",FACE,{"disambiguationData":[OSD([sQuery(id+"F0.wireOp",EDGE,"E25.0"),sQuery(id+"F0.wireOp",EDGE,"E25.1"),sQuery(id+"F0.wireOp",EDGE,"E25.2"),sQuery(id+"F0.wireOp",EDGE,"E25.3"),sQuery(id+"F0.wireOp",EDGE,"E25.4"),sQuery(id+"F0.wireOp",EDGE,"E25.5"),sQuery(id+"F0.wireOp",EDGE,"E25.6"),sQuery(id+"F0.wireOp",EDGE,"E25.7")])],"isStart":false})})});
            extrude(context, id + "F13", {"entities" : qUnion([Q0]), "operationType" : NewBodyOperationType.REMOVE, "endBound" : BoundingType.UP_TO_SURFACE, "endBoundEntityFace" : qUnion([Q1]), "depth" : 25 * mm});
        }
        {
            var Q0;
            Q0=makeQuery(id+"F3.boolean.opBoolean","COPY",EDGE,{"derivedFrom":makeQuery(id+"F3.opExtrude","CAP_EDGE",EDGE,{"disambiguationData":[OSD([sQuery(id+"F0.wireOp",EDGE,"E25.6")])],"isStart":false})});
            var Q1;
            Q1=makeQuery(id+"F8.boolean.opBoolean","INTERSECT",EDGE,{"derivedFrom":[makeQuery(id+"F5.opExtrude","SWEPT_FACE",FACE,{"disambiguationData":[OSD([sQuery(id+"F4.wireOp",EDGE,"E30")])]}),makeQuery(id+"F8.opExtrude","CAP_FACE",FACE,{"disambiguationData":[OSD([sQuery(id+"F7.wireOp",EDGE,"E67")])],"isStart":false})]});
            var Q2;
            Q2=makeQuery(id+"F8.boolean.opBoolean","INTERSECT",EDGE,{"disambiguationData":[OD(1.0)],"derivedFrom":[makeQuery(id+"F5.opExtrude","SWEPT_FACE",FACE,{"disambiguationData":[OSD([sQuery(id+"F4.wireOp",EDGE,"E30")])]}),makeQuery(id+"F8.opExtrude","SWEPT_FACE",FACE,{"disambiguationData":[OSD([sQuery(id+"F7.wireOp",EDGE,"E67")])]})]});
            var Q3;
            {var subQ0=sQuery(id+"F4.wireOp",EDGE,"E30");Q3=makeQuery(id+"F8.boolean.opBoolean","SPLIT",EDGE,{"disambiguationData":[TD([makeQuery(id+"F5.opExtrude","SWEPT_FACE",FACE,{"disambiguationData":[OSD([sQuery(id+"F4.wireOp",EDGE,"E35.filletArc")])]})])],"derivedFrom":makeQuery(id+"F5.opExtrude","CAP_EDGE",EDGE,{"disambiguationData":[OSD([subQ0])],"isStart":false})});}
            var Q4;
            {var subQ0=sQuery(id+"F0.wireOp",EDGE,"E25.7");var subQ1=sQuery(id+"F0.wireOp",EDGE,"E25.1");var subQ2=sQuery(id+"F0.wireOp",EDGE,"E25.6");var subQ3=sQuery(id+"F0.wireOp",EDGE,"E25.5");var subQ4=sQuery(id+"F0.wireOp",EDGE,"E25.4");var subQ5=sQuery(id+"F0.wireOp",EDGE,"E25.0");var subQ6=sQuery(id+"F0.wireOp",EDGE,"E25.2");var subQ7=sQuery(id+"F0.wireOp",EDGE,"E25.3");Q4=makeQuery(id+"F8.boolean.opBoolean","INTERSECT",EDGE,{"derivedFrom":[makeQuery(id+"F5.boolean.opBoolean","SPLIT",FACE,{"disambiguationData":[TD([makeQuery(id+"F2.opExtrude","SWEPT_FACE",FACE,{"disambiguationData":[OSD([subQ5])]})])],"derivedFrom":makeQuery(id+"F3.boolean.opBoolean","COPY",FACE,{"derivedFrom":makeQuery(id+"F3.opExtrude","CAP_FACE",FACE,{"disambiguationData":[OSD([subQ5,subQ1,subQ6,subQ7,subQ4,subQ3,subQ2,subQ0])],"isStart":false})})}),makeQuery(id+"F8.opExtrude","SWEPT_FACE",FACE,{"disambiguationData":[OSD([sQuery(id+"F7.wireOp",EDGE,"E67")])]})]});}
            var Q5;
            Q5=makeQuery(id+"F8.boolean.opBoolean","INTERSECT",EDGE,{"disambiguationData":[OD(0.0)],"derivedFrom":[makeQuery(id+"F5.opExtrude","SWEPT_FACE",FACE,{"disambiguationData":[OSD([sQuery(id+"F4.wireOp",EDGE,"E30")])]}),makeQuery(id+"F8.opExtrude","SWEPT_FACE",FACE,{"disambiguationData":[OSD([sQuery(id+"F7.wireOp",EDGE,"E67")])]})]});
            fillet(context, id + "F14", {"entities" : qUnion([Q0, Q1, Q2, Q3, Q4, Q5]), "radius" : 3 * mm, "tangentPropagation" : true, "allowEdgeOverflow" : false});
        }
        {
            var Q0;
            Q0=makeQuery(id+"F1.opExtrude","CAP_EDGE",EDGE,{"disambiguationData":[OSD([sQuery(id+"F0.wireOp",EDGE,"E1.bottom")])],"isStart":false});
            fillet(context, id + "F15", {"entities" : qUnion([Q0]), "radius" : 2 * mm, "tangentPropagation" : true, "allowEdgeOverflow" : false});
        }
        {
            var Q0;
            {var subQ0=sQuery(id+"F0.wireOp",EDGE,"E22.filletArc");var subQ1=sQuery(id+"F0.wireOp",EDGE,"E7");var subQ2=sQuery(id+"F0.wireOp",EDGE,"E6");var subQ3=sQuery(id+"F0.wireOp",EDGE,"E5");var subQ4=sQuery(id+"F0.wireOp",EDGE,"E4");var subQ5=sQuery(id+"F0.wireOp",EDGE,"E1.bottom");var subQ6=sQuery(id+"F0.wireOp",EDGE,"E21.filletArc");var subQ7=sQuery(id+"F0.wireOp",EDGE,"E1.top");var subQ8=sQuery(id+"F0.wireOp",EDGE,"E1.left");var subQ9=sQuery(id+"F0.wireOp",EDGE,"E1.right");var subQ10=sQuery(id+"F0.wireOp",EDGE,"E23.filletArc");var subQ11=sQuery(id+"F0.wireOp",EDGE,"E24.filletArc");Q0=makeQuery(id+"F2.boolean.opBoolean","SPLIT",FACE,{"disambiguationData":[TD([makeQuery(id+"F1.opExtrude","SWEPT_FACE",FACE,{"disambiguationData":[OSD([subQ5])]})])],"derivedFrom":makeQuery(id+"F1.opExtrude","CAP_FACE",FACE,{"disambiguationData":[OSD([subQ5,subQ7,subQ8,subQ9,subQ4,subQ3,subQ2,subQ1,subQ6,subQ0,subQ10,subQ11])],"isStart":true})});}
            var sketch = newSketch(context, id + "F16", { "sketchPlane" : qUnion([Q0])});
            skLineSegment(sketch, "E79.0", {"start": v(-64.25, 74.25) * mm, "end": v(64.25, 74.25) * mm});
            skPoint(sketch, "E80.endSnap0", {"position": v(0, 89.25) * mm});
            skLineSegment(sketch, "E81", {"start": v(13.14, 104.25) * mm, "end": v(13.14, 92.25) * mm});
            skLineSegment(sketch, "E82", {"start": v(13.14, 92.25) * mm, "end": v(31.14, 74.25) * mm});
            skArc(sketch, "E83", {"start": v(13.14, 104.25) * mm, "mid": v(-1.99, 119.25) * mm, "end": v(-16.86, 104) * mm});
            skCircle(sketch, "E84", {"center": v(-1.86, 104.25) * mm, "radius": 6 * mm});
            skLineSegment(sketch, "E85", {"start": v(-16.86, 104) * mm, "end": v(-16.65, 92) * mm});
            skLineSegment(sketch, "E86", {"start": v(-16.65, 92) * mm, "end": v(-34.4, 74.25) * mm});
            skLineSegment(sketch, "E87", {"start": v(0, 0) * mm, "end": v(-108.8, 0) * mm, "construction": true});
            skLineSegment(sketch, "E88.MirrorCS", {"start": v(13.14, -104.25) * mm, "end": v(13.14, -92.25) * mm});
            skCircle(sketch, "E89.MirrorC", {"center": v(-1.86, -104.25) * mm, "radius": 6 * mm});
            skLineSegment(sketch, "E90.MirrorCS", {"start": v(-16.86, -104) * mm, "end": v(-16.65, -92) * mm});
            skLineSegment(sketch, "E91.MirrorCS", {"start": v(-16.65, -92) * mm, "end": v(-34.4, -74.25) * mm});
            skLineSegment(sketch, "E92.MirrorCS", {"start": v(13.14, -92.25) * mm, "end": v(31.14, -74.25) * mm});
            skArc(sketch, "E93.MirrorCS", {"start": v(13.14, -104.25) * mm, "mid": v(-1.99, -119.25) * mm, "end": v(-16.86, -104) * mm});
            skPoint(sketch, "E94.MirrorP", {"position": v(0, -89.25) * mm});
            skSolve(sketch);
        }
        {
            var Q0;
            Q0=makeQuery(id+"F16.imprint","IMPRINT",FACE,{"disambiguationData":[TD([[makeQuery(id+"F16.imprint","IMPRINT",EDGE,{"derivedFrom":makeQuery(id+"F1.opExtrude","CAP_EDGE",EDGE,{"disambiguationData":[OSD([sQuery(id+"F0.wireOp",EDGE,"E1.left")])],"isStart":true})}),-1.0]])]});
            var Q1;
            Q1=makeQuery(id+"F16.imprint","IMPRINT",FACE,{"disambiguationData":[TD([[makeQuery(id+"F16.imprint","IMPRINT",EDGE,{"derivedFrom":sQuery(id+"F16.wireOp",EDGE,"E88.MirrorCS")}),1.0]])]});
            var Q2;
            Q2=makeQuery(id+"F16.imprint","IMPRINT",FACE,{"disambiguationData":[TD([[makeQuery(id+"F16.imprint","IMPRINT",EDGE,{"derivedFrom":sQuery(id+"F16.wireOp",EDGE,"E81")}),-1.0]])]});
            var Q3;
            Q3=makeQuery(id+"F2.opExtrude","CAP_FACE",FACE,{"disambiguationData":[OSD([sQuery(id+"F0.wireOp",EDGE,"E12"),sQuery(id+"F0.wireOp",EDGE,"E13"),sQuery(id+"F0.wireOp",EDGE,"E14"),sQuery(id+"F0.wireOp",EDGE,"E15"),sQuery(id+"F0.wireOp",EDGE,"E17.filletArc"),sQuery(id+"F0.wireOp",EDGE,"E18.filletArc"),sQuery(id+"F0.wireOp",EDGE,"E19.filletArc"),sQuery(id+"F0.wireOp",EDGE,"E20.filletArc"),sQuery(id+"F0.wireOp",EDGE,"E25.0"),sQuery(id+"F0.wireOp",EDGE,"E25.1"),sQuery(id+"F0.wireOp",EDGE,"E25.2"),sQuery(id+"F0.wireOp",EDGE,"E25.3"),sQuery(id+"F0.wireOp",EDGE,"E25.4"),sQuery(id+"F0.wireOp",EDGE,"E25.5"),sQuery(id+"F0.wireOp",EDGE,"E25.6"),sQuery(id+"F0.wireOp",EDGE,"E25.7")])],"isStart":false});
            extrude(context, id + "F17", {"entities" : qUnion([Q0, Q1, Q2]), "operationType" : NewBodyOperationType.ADD, "endBound" : BoundingType.UP_TO_SURFACE, "endBoundEntityFace" : qUnion([Q3]), "depth" : 25 * mm});
        }
    });
